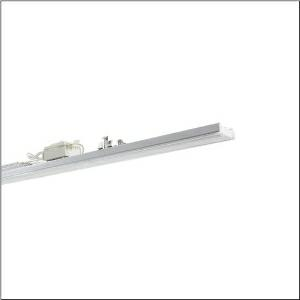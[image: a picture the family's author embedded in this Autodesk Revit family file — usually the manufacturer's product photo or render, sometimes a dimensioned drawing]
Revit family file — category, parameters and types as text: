
# Revit family: licross_r__11_recessed_mo_51te12dn4axg3s4_42bd
name_source: partatom
category: Lighting Fixtures
units: mm (PartAtom-declared; Revit-internal decimal feet)

## family parameters
Cut with Voids When Loaded = No
Host = Face
Light Source = No
Part Type = Normal
Room Calculation Point = No
Round Connector Dimension = Use Diameter
Shared = No

## types (1)
- --- (1 x LED, 1010 lm, 6.7 W, 4000K)
    Apparent Load = 7 VA
    CIE Flux Codes = 67 92 99 100 100
    Color Rendering = 80
    Color Temperature = 4000K
    Default Elevation = 1800 mm
    Description = Licross® 11 Recessed MO, luminaire insert, of sheet steel, galvanised, coil coated, white, length: 1.500mm, width: 66mm, height: 67mm, LED rated luminous flux: 10.240lm, light colour: 840, control gear: DALI 2, with plug, 6-pole, with phase selection, for trunking rail, 9 or 11-core, mains connection: 220..240V, AC, 50/60Hz, rated input power: 61W, for trunking rail, 9-/11-core, internal wiring halogen-free, for emergency light function, converter,control gear: single battery element, battery: LiFePO4, 9Ah, primary optical cover: cover, of PMMA, light emission: direct distribution, primary light characteristic: symmetric, protection rating (complete): IP54, insulation class (complete): insulation class I (protective earthing), certification: CE, UKCA, protection symbol: D if used in an environment with non-conductive dust loads with corresponding accessories, impact resistance: IK06, permissible ambient temperature for indoor applications: +5..+35°C, standard: EN 60598-2-22, LABS conformity tested according to VDMA 24364:2018-05, reducing of maximum allowable ambient temperature of 5°C with ceiling mounting, corresponds to IFS (International Featured Standards) requirements for safety and quality in the food industry, packaging unit: 1 piece
    Height = 58 mm
    Lamp = 1 x LED
    Lamp Light Flux = 1010 lm
    Lamp Power = 6.7 W
    Lamp count = 1
    Length = 1500 mm
    Luminous efficacy = 151 lm/W
    Manufacturer = Siteco
    ModVariant = No
    Model = 51TE12DN4AXG3S4
    Mounting Place = Ceiling
    Mounting Type = Pendant
    Number of Poles = 1
    OnlyDefault = Yes
    Power Factor = 1
    Product Name = Licross® 11 Recessed MO
    Product group = luminaire insert | ceiling pendant
    ProductGroupID = 902
    Protection Class = Protection class I
    Protection Degree = IP 54
    RLX_Detail_Level = 1
    RLX_Emergency_Light_Flux = 0 lm
    RLX_Emergency_Type = 0
    RLX_Emergency_Type_DB = No
    RlxData = <blob elided: 24849 chars, md5=ac00a3c0>
    Socket = socket
    Standby Power = 0 W
    System Light Flux = 1010 lm
    System Power = 7 W
    Type Comments = : emergency light operation: 3 h
    Type Image = l_1296930.jpg
    URL = http://relux.com
    VarID = @adj_111681
    Voltage = 0 V
    Weight = 0.00 kg
    Width = 66 mm

## geometry (parser evidence)
native form markers: Blend x4, Sweep x12
no freeform markers — native parametric forms only
